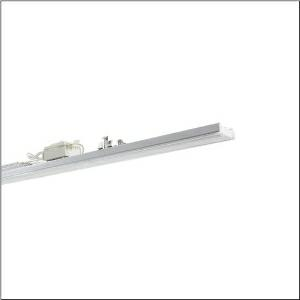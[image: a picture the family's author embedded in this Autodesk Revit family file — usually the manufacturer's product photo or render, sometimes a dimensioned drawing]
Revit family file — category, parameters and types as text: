
# Revit family: licross_11_recessed_ho_51te18dn4d5m
name_source: partatom
category: Lighting Fixtures
units: mm (PartAtom-declared; Revit-internal decimal feet)

## family parameters
Cut with Voids When Loaded = No
Host = Face
Light Source = No
Part Type = Normal
Room Calculation Point = No
Round Connector Dimension = Use Diameter
Shared = No

## types (1)
- --- (1 x LED, 13890 lm, 76.8 W, 4000K)
    Apparent Load = 77 VA
    CIE Flux Codes = 78 94 99 100 100
    Color Rendering = 80
    Color Temperature = 4000K
    Default Elevation = 1800 mm
    Description = Licross 11 Recessed HO, luminaire insert, of sheet steel, galvanised, coil coated, white, length: 1.500mm, width: 66mm, height: 67mm, LED rated luminous flux: 13.890lm, light colour: 840, SDCM (Standard Deviation of Colour Matching)MacAdam ≤ 2 SDCM (initial), control gear: DALI 2, with plug, 5-pole, with phase selection, mains connection: 220..240V, AC, 50/60Hz, rated input power: 77W, internal wiring halogen-free, primary light control with lens, of plastic, primary optical cover: cover, of PMMA, light emission: direct distribution, primary light characteristic: symmetric, protection rating (complete): IP54, insulation class (complete): insulation class I (protective earthing), certification: CE, ENEC, VDE, UKCA, protection symbol: D if used in an environment with non-conductive dust loads with corresponding accessories, impact resistance: IK06, permissible ambient temperature for indoor applications: -25..+30°C, corresponds to IFS (International Featured Standards) requirements for safety and quality in the food industry, reducing of maximum allowable ambient temperature of 5°C with ceiling mounting, LABS conformity tested according to VDMA 24364:2018-05, The light source and the operating device comply with the requirements of the Ecodesign Regulation (EU) 2019/2020 and are replaceable in accordance with this regulation, packaging unit: 1 piece
    Height = 58 mm
    Lamp = 1 x LED
    Lamp Light Flux = 13890 lm
    Lamp Power = 76.8 W
    Lamp count = 1
    Length = 1500 mm
    Luminous efficacy = 181 lm/W
    Manufacturer = Siteco
    ModVariant = No
    Model = 51TE18DN4D5M
    Mounting Place = Ceiling
    Mounting Type = Pendant
    Number of Poles = 1
    OnlyDefault = Yes
    Power Factor = 1
    Product Name = Licross 11 Recessed HO
    Product group = luminaire insert | ceiling pendant
    ProductGroupID = 901
    Protection Class = Protection class I
    Protection Degree = IP 54
    RLX_Detail_Level = 1
    RLX_Emergency_Light_Flux = 0 lm
    RLX_Emergency_Type = 0
    RLX_Emergency_Type_DB = No
    RlxData = <blob elided: 24937 chars, md5=1099b55a>
    Socket = socket
    Standby Power = 0 W
    System Light Flux = 13890 lm
    System Power = 77 W
    Type Comments = factory setting: luminous flux: 100 % | dim-lin: 254 | 522 mA
    Type Image = l_1296930.jpg
    URL = http://relux.com
    VarID = @adj_100943
    Voltage = 0 V
    Weight = 0.00 kg
    Width = 66 mm

## geometry (parser evidence)
native form markers: Blend x4, Sweep x11
no freeform markers — native parametric forms only
